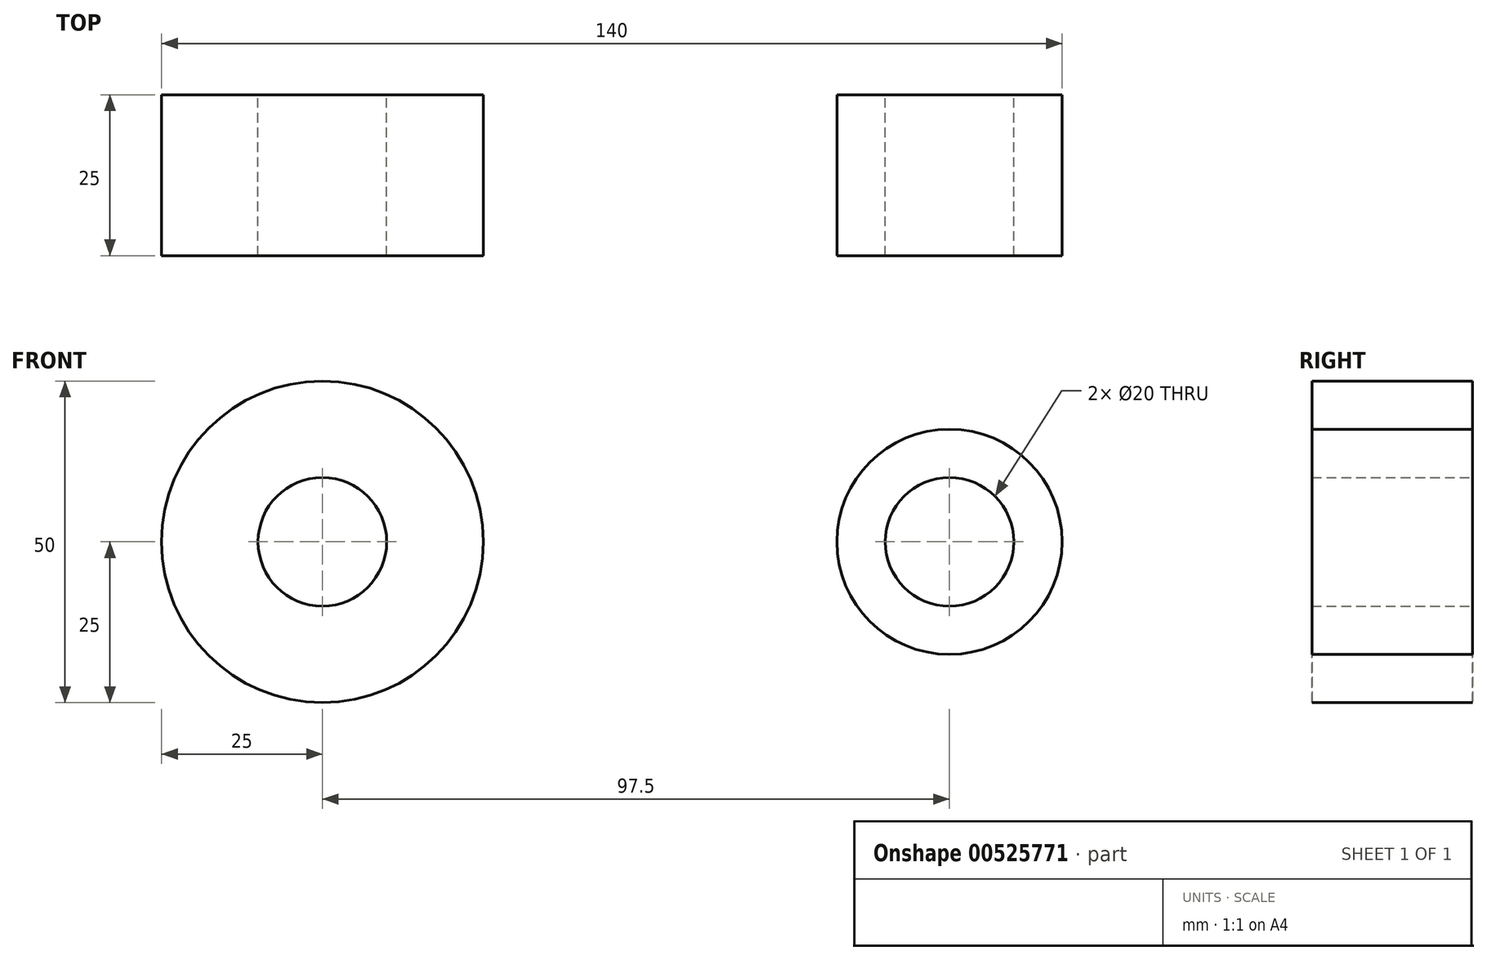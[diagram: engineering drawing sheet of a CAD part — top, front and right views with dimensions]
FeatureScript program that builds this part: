
annotation { "Feature Type Name" : "Feature", "Feature Type Description" : "" }
export const myFeature = defineFeature(function(context is Context, id is Id, definition is map)
    precondition{}
    {
        {
            var Q0;
            Q0=qCreatedBy(makeId("Front.planeOp"),FACE);
            var sketch = newSketch(context, id + "F0", { "sketchPlane" : qUnion([Q0])});
            skCircle(sketch, "E0", {"center": v(0, 0) * mm, "radius": 25 * mm});
            skCircle(sketch, "E1", {"center": v(97.5, 0) * mm, "radius": 17.5 * mm});
            skLineSegment(sketch, "E2", {"start": v(1.92, -24.93) * mm, "end": v(98.85, -17.45) * mm});
            skLineSegment(sketch, "E3", {"start": v(98.85, -17.45) * mm, "end": v(1.92, -24.93) * mm});
            skLineSegment(sketch, "E4", {"start": v(1.92, 24.93) * mm, "end": v(98.85, 17.45) * mm});
            skCircle(sketch, "E5", {"center": v(0, 0) * mm, "radius": 10 * mm});
            skCircle(sketch, "E6", {"center": v(97.5, 0) * mm, "radius": 10 * mm});
            skSolve(sketch);
        }
        {
            var Q0;
            Q0=makeQuery(id+"F0.imprint","IMPRINT",FACE,{"disambiguationData":[TD([[makeQuery(id+"F0.imprint","IMPRINT",EDGE,{"derivedFrom":sQuery(id+"F0.wireOp",EDGE,"E6")}),-1.0]])]});
            var Q1;
            Q1=makeQuery(id+"F0.imprint","IMPRINT",FACE,{"disambiguationData":[TD([[makeQuery(id+"F0.imprint","IMPRINT",EDGE,{"derivedFrom":sQuery(id+"F0.wireOp",EDGE,"E5")}),-1.0]])]});
            var Q2;
            {var subQ0=sQuery(id+"F0.wireOp",EDGE,"E3");Q2=makeQuery(id+"F0.imprint","IMPRINT",FACE,{"disambiguationData":[TD([[makeQuery(id+"F0.imprint","IMPRINT",EDGE,{"derivedFrom":subQ0}),-1.0]])]});}
            extrude(context, id + "F1", {"entities" : qUnion([Q0, Q1, Q2]), "depth" : 25 * mm, "offsetDistance" : 25 * mm});
        }
    });
